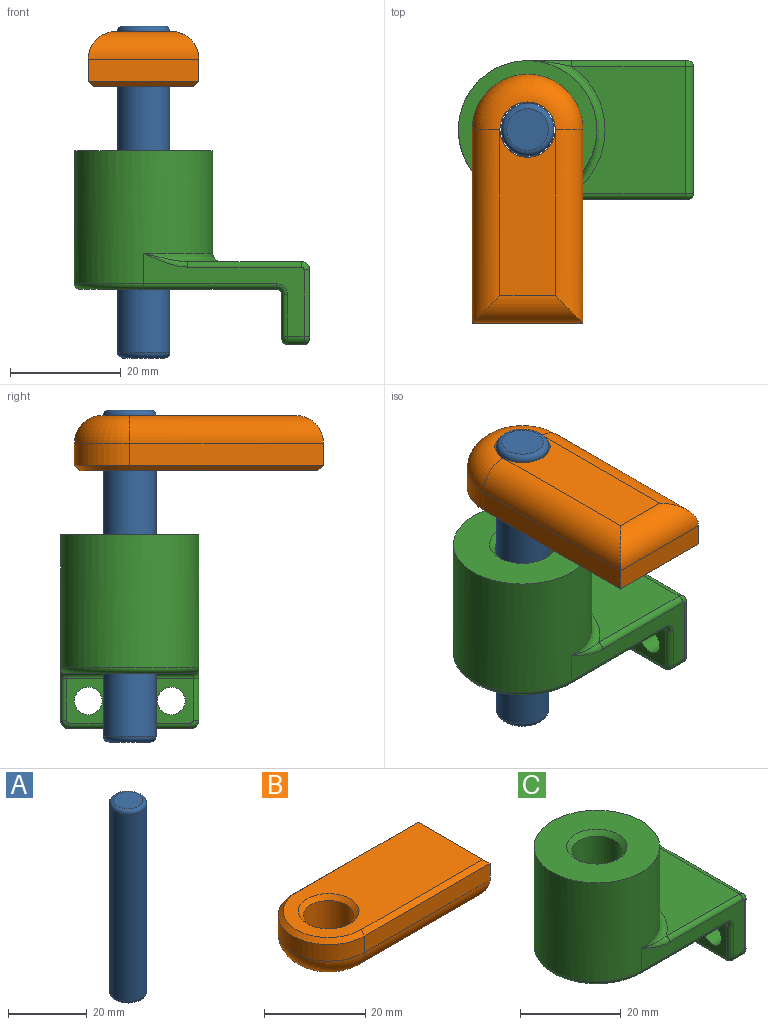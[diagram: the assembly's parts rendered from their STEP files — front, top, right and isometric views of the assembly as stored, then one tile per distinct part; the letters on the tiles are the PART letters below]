
ASSEMBLY  parts=3 mates=2
PART A: 5 faces, bbox 10.3x10.3x60 mm
  f0: cylinder r=4.75mm len=58mm, axis (0,0,-1), area 1731mm2, adj f3,f4
  f1: plane 7.5x7.5mm, normal (0,0,1), area 44.2mm2, adj f4
  f2: plane 7.5x7.5mm, normal (0,0,-1), area 44.2mm2, adj f3
  f3: torus R=3.75mm, axis (0,0,1), area 43.3mm2, adj f0,f2
  f4: torus R=3.75mm, axis (0,0,1), area 43.3mm2, adj f0,f1
PART B: 16 faces, bbox 45.8x21.6x10 mm
  f0: plane 35x4mm, normal (0,1,0), area 140mm2, adj f1,f3,f9,f15
  f1: cylinder r=10mm len=20mm, axis (0,0,-1), area 125.7mm2, adj f0,f2,f11,f13
  f2: plane 35x4mm, normal (0,-1,0), area 140mm2, adj f1,f3,f10,f12
  f3: plane 20x4mm, normal (1,0,0), area 80mm2, adj f0,f2,f8,f14
  f4: cylinder r=5mm len=10mm, axis (0,0,-1), area 282.7mm2, adj f6,f7,f13
  f5: plane 43x18mm, normal (0,0,1), area 626.1mm2, adj f7,f8,f9,f10,f11
  f6: plane 30x10mm, normal (0,0,-1), area 260.7mm2, adj f4,f12,f14,f15
  f7: cone r=5mm half-angle=45deg, axis (0,0,1), area 48.9mm2, adj f4,f5
  f8: plane 20x1mm, normal (0.71,0,0.71), area 26.9mm2, adj f3,f5,f9,f10
  f9: plane 35x1mm, normal (0,0.71,0.71), area 48.8mm2, adj f0,f5,f8,f11
  f10: plane 35x1mm, normal (0,-0.71,0.71), area 48.8mm2, adj f2,f5,f8,f11
  f11: cone r=9mm half-angle=45deg, axis (0,0,-1), area 42.2mm2, adj f1,f5,f9,f10
  f12: cylinder r=5mm len=35mm, axis (1,0,0), area 260.6mm2, adj f2,f6,f13,f14
  f13: torus R=5mm, axis (0,0,1), area 201.9mm2, adj f1,f4,f12,f15
  f14: cylinder r=5mm len=20mm, axis (0,1,0), area 128.5mm2, adj f3,f6,f12,f15
  f15: cylinder r=5mm len=35mm, axis (-1,0,0), area 260.6mm2, adj f0,f6,f13,f14
PART C: 40 faces, bbox 43.5x32.6x35 mm
  f0: plane 35.5x23mm, normal (0,0,-1), area 646.6mm2, adj f27,f28,f30,f31,f39
  f1: plane 23x20.52mm, normal (0,0,1), area 374.8mm2, adj f14,f15,f17,f25
  f2: plane 29x15mm, normal (0,1,0), area 123.8mm2, adj f3,f13,f23,f24,f25,f26,f30,f33
  f3: cylinder r=12.5mm len=25mm, axis (0,0,-1), area 1669mm2, adj f2,f4,f7,f14,f28
  f4: plane 29x15mm, normal (0,-1,0), area 123.8mm2, adj f3,f12,f16,f17,f18,f19,f27,f29
  f5: plane 23x12.5mm, normal (1,0,0), area 248.1mm2, adj f10,f11,f15,f19,f20,f21,f22,f23
  f6: cylinder r=5mm len=23mm, axis (0,0,-1), area 722.6mm2, adj f38,f39
  f7: plane 25x25mm, normal (0,0,1), area 377.8mm2, adj f3,f38
  f8: plane 23x8mm, normal (-1,0,0), area 144.6mm2, adj f10,f11,f31,f32,f34,f35,f36,f37
  f9: plane 22x3mm, normal (0,0,-1), area 66mm2, adj f12,f13,f21,f36
  f10: cylinder r=2.5mm len=5mm, axis (1,0,0), area 78.5mm2, adj f5,f8
  f11: cylinder r=2.5mm len=5mm, axis (1,0,0), area 78.5mm2, adj f5,f8
  f12: cylinder r=1.5mm len=3mm, axis (1,0,0), area 7.1mm2, adj f4,f9,f20,f34
  f13: cylinder r=1.5mm len=3mm, axis (-1,0,0), area 7.1mm2, adj f2,f9,f22,f37
  f14: torus R=14mm, axis (0,0,1), area 75.7mm2, adj f1,f3,f16,f26
  f15: cylinder r=1.5mm len=23mm, axis (0,-1,0), area 54.2mm2, adj f1,f5,f18,f24
  f16: bspline ~8.33x2.5mm, area 6.4mm2, adj f4,f14,f17
  f17: cylinder r=1mm len=20.52mm, axis (-1,0,0), area 32.2mm2, adj f1,f4,f16,f18
  f18: torus R=0.5mm, axis (0,-1,0), area 2.8mm2, adj f4,f15,f17,f19
  f19: cylinder r=1mm len=12mm, axis (0,0,1), area 18.8mm2, adj f4,f5,f18,f20
  f20: torus R=0.5mm, axis (-1,0,0), area 2.8mm2, adj f5,f12,f19,f21
  f21: cylinder r=1mm len=22mm, axis (0,-1,0), area 34.6mm2, adj f5,f9,f20,f22
  f22: torus R=0.5mm, axis (-1,0,0), area 2.8mm2, adj f5,f13,f21,f23
  f23: cylinder r=1mm len=12mm, axis (0,0,-1), area 18.8mm2, adj f2,f5,f22,f24
  f24: torus R=0.5mm, axis (0,-1,0), area 2.8mm2, adj f2,f15,f23,f25
  f25: cylinder r=1mm len=20.52mm, axis (1,0,0), area 32.2mm2, adj f1,f2,f24,f26
  f26: bspline ~8.33x2.5mm, area 6.4mm2, adj f2,f14,f25
  f27: cylinder r=1mm len=24mm, axis (1,0,0), area 37.7mm2, adj f0,f4,f28,f29
  f28: torus R=11.5mm, axis (0,0,1), area 59.9mm2, adj f0,f3,f27,f30
  f29: torus R=2mm, axis (0,-1,0), area 3.4mm2, adj f4,f27,f31,f32
  f30: cylinder r=1mm len=24mm, axis (-1,0,0), area 37.7mm2, adj f0,f2,f28,f33
  f31: cylinder r=1mm len=23mm, axis (0,-1,0), area 36.1mm2, adj f0,f8,f29,f33
  f32: cylinder r=1mm len=7.5mm, axis (0,0,1), area 11.8mm2, adj f4,f8,f29,f34
  f33: torus R=2mm, axis (0,-1,0), area 3.4mm2, adj f2,f30,f31,f35
  f34: torus R=0.5mm, axis (1,0,0), area 2.8mm2, adj f8,f12,f32,f36
  f35: cylinder r=1mm len=7.5mm, axis (0,0,-1), area 11.8mm2, adj f2,f8,f33,f37
  f36: cylinder r=1mm len=22mm, axis (0,-1,0), area 34.6mm2, adj f8,f9,f34,f37
  f37: torus R=0.5mm, axis (1,0,0), area 2.8mm2, adj f8,f13,f35,f36
  f38: cone r=5mm half-angle=45deg, axis (0,0,1), area 48.9mm2, adj f6,f7
  f39: cone r=6mm half-angle=45deg, axis (0,0,-1), area 48.9mm2, adj f0,f6
PLACE A t=(-26.08,-12.82,-25.03)mm
PLACE B rot(axis=(0.71,-0.71,0),180deg) t=(-25.21,-21.81,33.97)mm
PLACE C t=(-11.08,-12.82,-12.6)mm fixed
MATE fastened A.f0 <-> B.f1  axis (0,0,1) through (-26.08,-12.82,33.97)mm
MATE slider A.f0 <-> C.f3  axis (0,0,-1) through (-26.08,-12.82,4.97)mm
